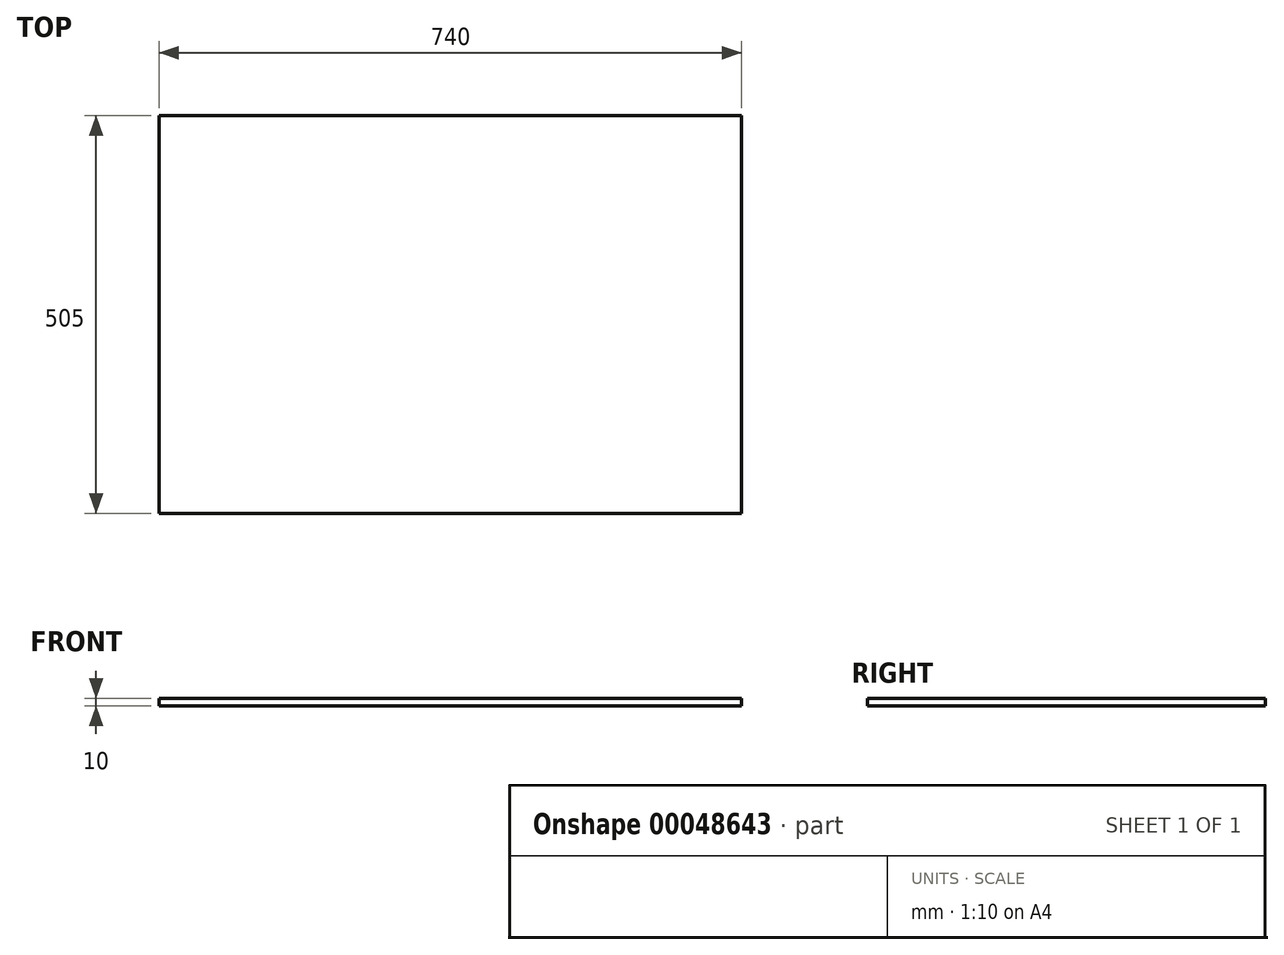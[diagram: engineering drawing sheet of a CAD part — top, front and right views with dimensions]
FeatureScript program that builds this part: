
annotation { "Feature Type Name" : "Feature", "Feature Type Description" : "" }
export const myFeature = defineFeature(function(context is Context, id is Id, definition is map)
    precondition{}
    {
        {
            var Q0;
            Q0=qCreatedBy(makeId("Top.planeOp"),FACE);
            var sketch = newSketch(context, id + "F0", { "sketchPlane" : qUnion([Q0])});
            skLineSegment(sketch, "E0.bottom", {"start": v(-55.86, -62.87) * mm, "end": v(684.14, -62.87) * mm});
            skLineSegment(sketch, "E0.top", {"start": v(-55.86, 442.13) * mm, "end": v(684.14, 442.13) * mm});
            skLineSegment(sketch, "E0.left", {"start": v(-55.86, -62.87) * mm, "end": v(-55.86, 442.13) * mm});
            skLineSegment(sketch, "E0.right", {"start": v(684.14, -62.87) * mm, "end": v(684.14, 442.13) * mm});
            skSolve(sketch);
        }
        {
            var Q0;
            Q0=makeQuery(id+"F0.imprint","IMPRINT",FACE,{"disambiguationData":[TD([[makeQuery(id+"F0.imprint","IMPRINT",EDGE,{"derivedFrom":sQuery(id+"F0.wireOp",EDGE,"E0.bottom")}),1.0]])]});
            extrude(context, id + "F1", {"entities" : qUnion([Q0]), "depth" : 10 * mm});
        }
    });
